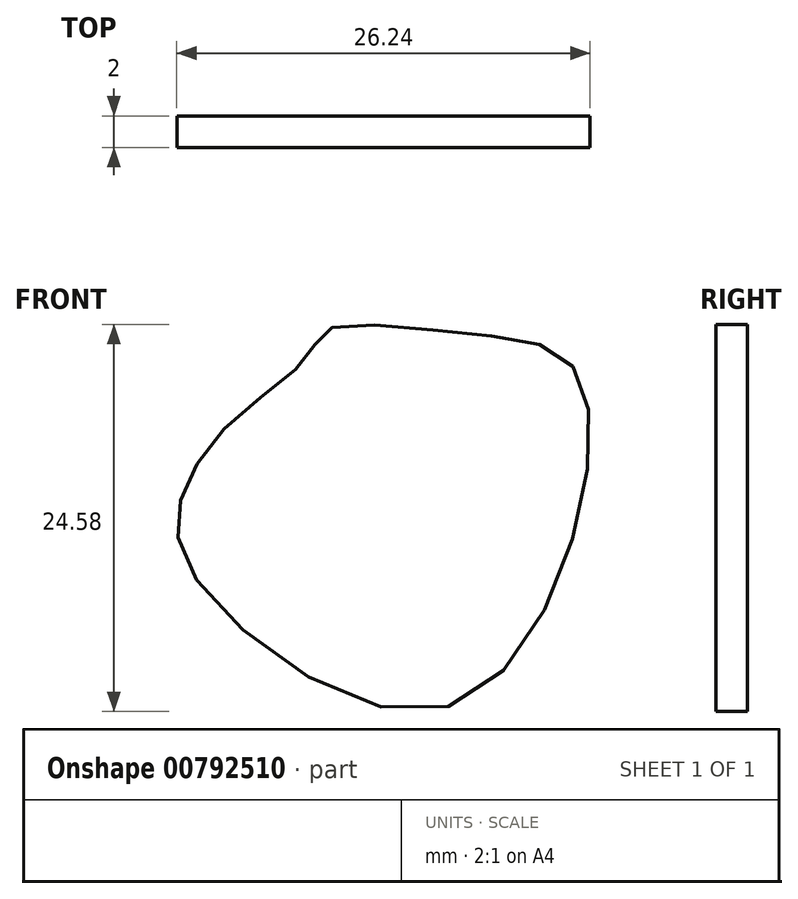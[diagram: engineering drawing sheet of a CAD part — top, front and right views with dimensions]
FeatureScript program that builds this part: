
annotation { "Feature Type Name" : "Feature", "Feature Type Description" : "" }
export const myFeature = defineFeature(function(context is Context, id is Id, definition is map)
    precondition{}
    {
        {
            var Q0;
            Q0=qCreatedBy(makeId("Front.planeOp"),FACE);
            var sketch = newSketch(context, id + "F0", { "sketchPlane" : qUnion([Q0])});
            skFitSpline(sketch, "E0", {"points": [v(-54.91, -44.95) * mm, v(-39.97, -53.25) * mm, v(-30.72, -41.15) * mm, v(-31.2, -31.2) * mm, v(-38.07, -29.3) * mm, v(-46.6, -29.06) * mm, v(-47.8, -30.72) * mm, v(-52.54, -34.75) * mm, v(-55.86, -39.73) * mm, v(-54.91, -44.95) * mm]});
            skSolve(sketch);
        }
        {
            var Q0;
            Q0=makeQuery(id+"F0.imprint","IMPRINT",FACE,{"disambiguationData":[TD([[makeQuery(id+"F0.imprint","IMPRINT",EDGE,{"derivedFrom":sQuery(id+"F0.wireOp",EDGE,"E0")}),1.0]])]});
            extrude(context, id + "F1", {"entities" : qUnion([Q0]), "depth" : 2 * mm, "offsetDistance" : 25 * mm});
        }
    });
